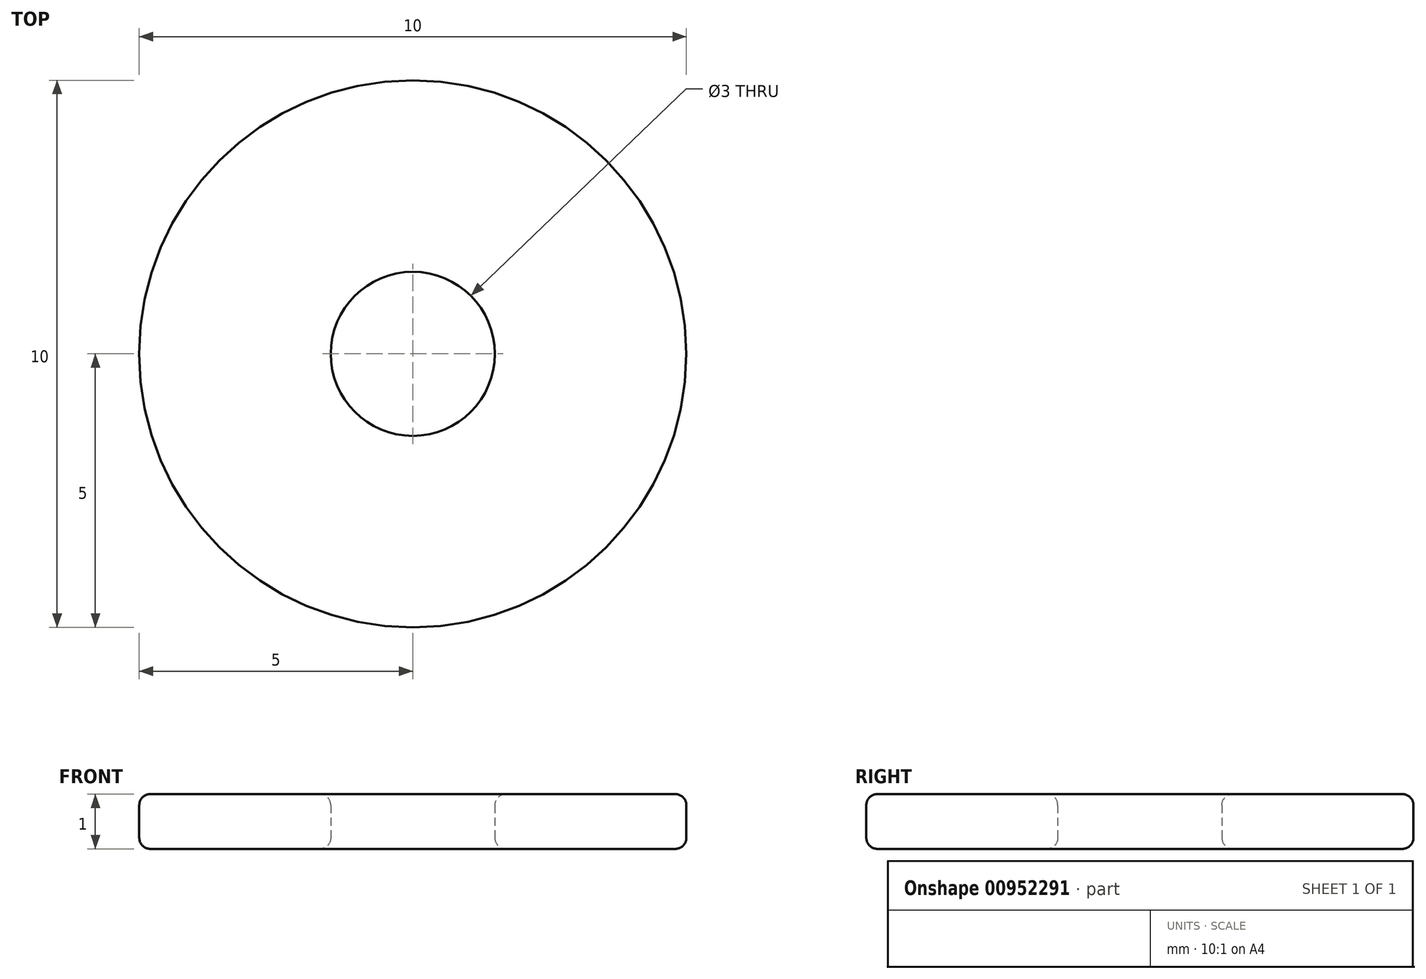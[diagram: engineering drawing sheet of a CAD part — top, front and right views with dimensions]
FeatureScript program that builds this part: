
annotation { "Feature Type Name" : "Feature", "Feature Type Description" : "" }
export const myFeature = defineFeature(function(context is Context, id is Id, definition is map)
    precondition{}
    {
        {
            var Q0;
            Q0=qCreatedBy(makeId("Top.planeOp"),FACE);
            cPlane(context, id + "F0", {"entities" : qUnion([Q0]), "cplaneType" : CPlaneType.OFFSET, "offset" : 0 * mm, "width" : 150 * mm, "height" : 150 * mm});
        }
        {
            var Q0;
            Q0=qCreatedBy(id+"F0.planeOp",FACE);
            var sketch = newSketch(context, id + "F1", { "sketchPlane" : qUnion([Q0])});
            skCircle(sketch, "E0", {"center": v(0, 0) * mm, "radius": 5 * mm});
            skCircle(sketch, "E1", {"center": v(0, 0) * mm, "radius": 1.5 * mm});
            skSolve(sketch);
        }
        {
            var Q0;
            Q0 = qSketchRegion(id + "F1", true);
            extrude(context, id + "F2", {"entities" : qUnion([Q0]), "depth" : 1 * mm, "offsetDistance" : 25 * mm});
        }
        {
            var Q0;
            Q0=makeQuery(id+"F2.opExtrude","CAP_FACE",FACE,{"disambiguationData":[OSD([sQuery(id+"F1.wireOp",EDGE,"E0"),sQuery(id+"F1.wireOp",EDGE,"E1")])],"isStart":false});
            var Q1;
            Q1=makeQuery(id+"F2.opExtrude","CAP_FACE",FACE,{"disambiguationData":[OSD([sQuery(id+"F1.wireOp",EDGE,"E0"),sQuery(id+"F1.wireOp",EDGE,"E1")])],"isStart":true});
            fillet(context, id + "F3", {"entities" : qUnion([Q0, Q1]), "tangentPropagation" : true, "radius" : 0.2 * mm, "defaultsChanged" : false, "vertexSettings" : [], "allowEdgeOverflow" : false});
        }
    });
